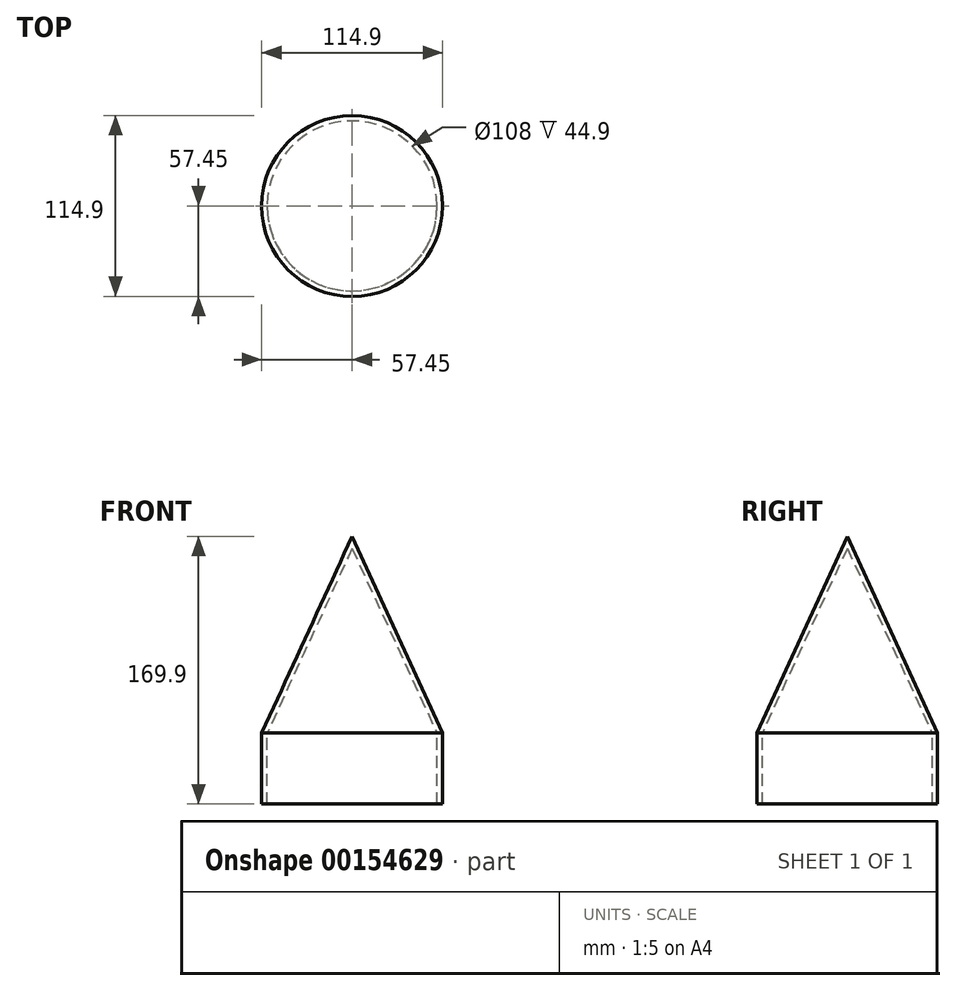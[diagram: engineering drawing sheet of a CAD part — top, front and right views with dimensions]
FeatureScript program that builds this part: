
annotation { "Feature Type Name" : "Feature", "Feature Type Description" : "" }
export const myFeature = defineFeature(function(context is Context, id is Id, definition is map)
    precondition{}
    {
        {
            var Q0;
            Q0=qCreatedBy(makeId("Front.planeOp"),FACE);
            var sketch = newSketch(context, id + "F0", { "sketchPlane" : qUnion([Q0])});
            skLineSegment(sketch, "E0", {"start": v(-57.45, 0.1) * mm, "end": v(0, 125) * mm});
            skLineSegment(sketch, "E1", {"start": v(0, 125) * mm, "end": v(0, 117.4) * mm});
            skLineSegment(sketch, "E2.0", {"start": v(-54, 0) * mm, "end": v(0, 117.4) * mm});
            skLineSegment(sketch, "E3.top", {"start": v(-57.45, -44.9) * mm, "end": v(-54, -44.9) * mm});
            skLineSegment(sketch, "E3.left", {"start": v(-57.45, 0.1) * mm, "end": v(-57.45, -44.9) * mm});
            skLineSegment(sketch, "E3.right", {"start": v(-54, 0.1) * mm, "end": v(-54, -44.9) * mm});
            skSolve(sketch);
        }
        {
            var Q0;
            Q0=makeQuery(id+"F0.imprint","IMPRINT",FACE,{"disambiguationData":[TD([[makeQuery(id+"F0.imprint","IMPRINT",EDGE,{"derivedFrom":sQuery(id+"F0.wireOp",EDGE,"E0")}),-1.0]])]});
            var Q1;
            Q1=sQuery(id+"F0.wireOp",EDGE,"E1");
            revolve(context, id + "F1", {"entities" : qUnion([Q0]), "axis" : qUnion([Q1]), "revolveType" : RevolveType.FULL});
        }
    });
